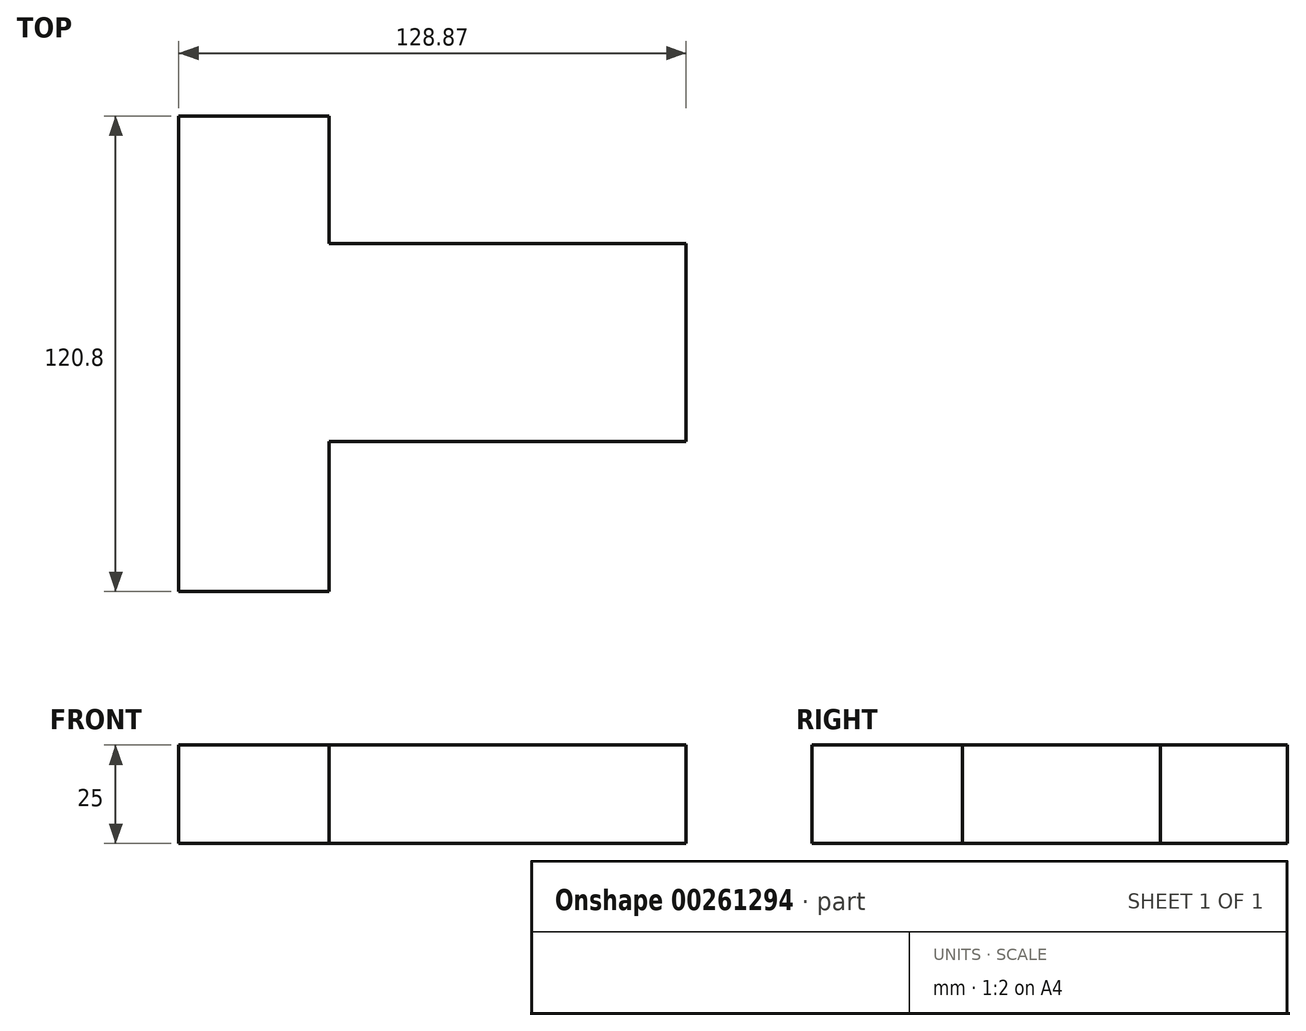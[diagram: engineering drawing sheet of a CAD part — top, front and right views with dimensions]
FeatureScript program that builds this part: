
annotation { "Feature Type Name" : "Feature", "Feature Type Description" : "" }
export const myFeature = defineFeature(function(context is Context, id is Id, definition is map)
    precondition{}
    {
        {
            var Q0;
            Q0=qCreatedBy(makeId("Top.planeOp"),FACE);
            var sketch = newSketch(context, id + "F0", { "sketchPlane" : qUnion([Q0])});
            skLineSegment(sketch, "E0.bottom", {"start": v(-45.35, 25.15) * mm, "end": v(45.35, 25.15) * mm});
            skLineSegment(sketch, "E0.top", {"start": v(-45.35, -25.15) * mm, "end": v(45.35, -25.15) * mm});
            skLineSegment(sketch, "E0.right", {"start": v(45.35, 25.15) * mm, "end": v(45.35, -25.15) * mm});
            skPoint(sketch, "E0.middle", {"position": v(0, 0) * mm});
            skLineSegment(sketch, "E1.bottom", {"start": v(-45.35, 57.48) * mm, "end": v(-83.52, 57.48) * mm});
            skLineSegment(sketch, "E1.top", {"start": v(-45.35, -63.32) * mm, "end": v(-83.52, -63.32) * mm});
            skLineSegment(sketch, "E1.left", {"start": v(-45.35, 57.48) * mm, "end": v(-45.35, 25.15) * mm});
            skLineSegment(sketch, "E1.right", {"start": v(-83.52, 57.48) * mm, "end": v(-83.52, -63.32) * mm});
            skLineSegment(sketch, "E2.trimOffspring", {"start": v(-45.35, -25.15) * mm, "end": v(-45.35, -63.32) * mm});
            skSolve(sketch);
        }
        {
            var Q0;
            Q0 = qSketchRegion(id + "F0", true);
            extrude(context, id + "F1", {"entities" : qUnion([Q0]), "depth" : 25 * mm});
        }
    });
